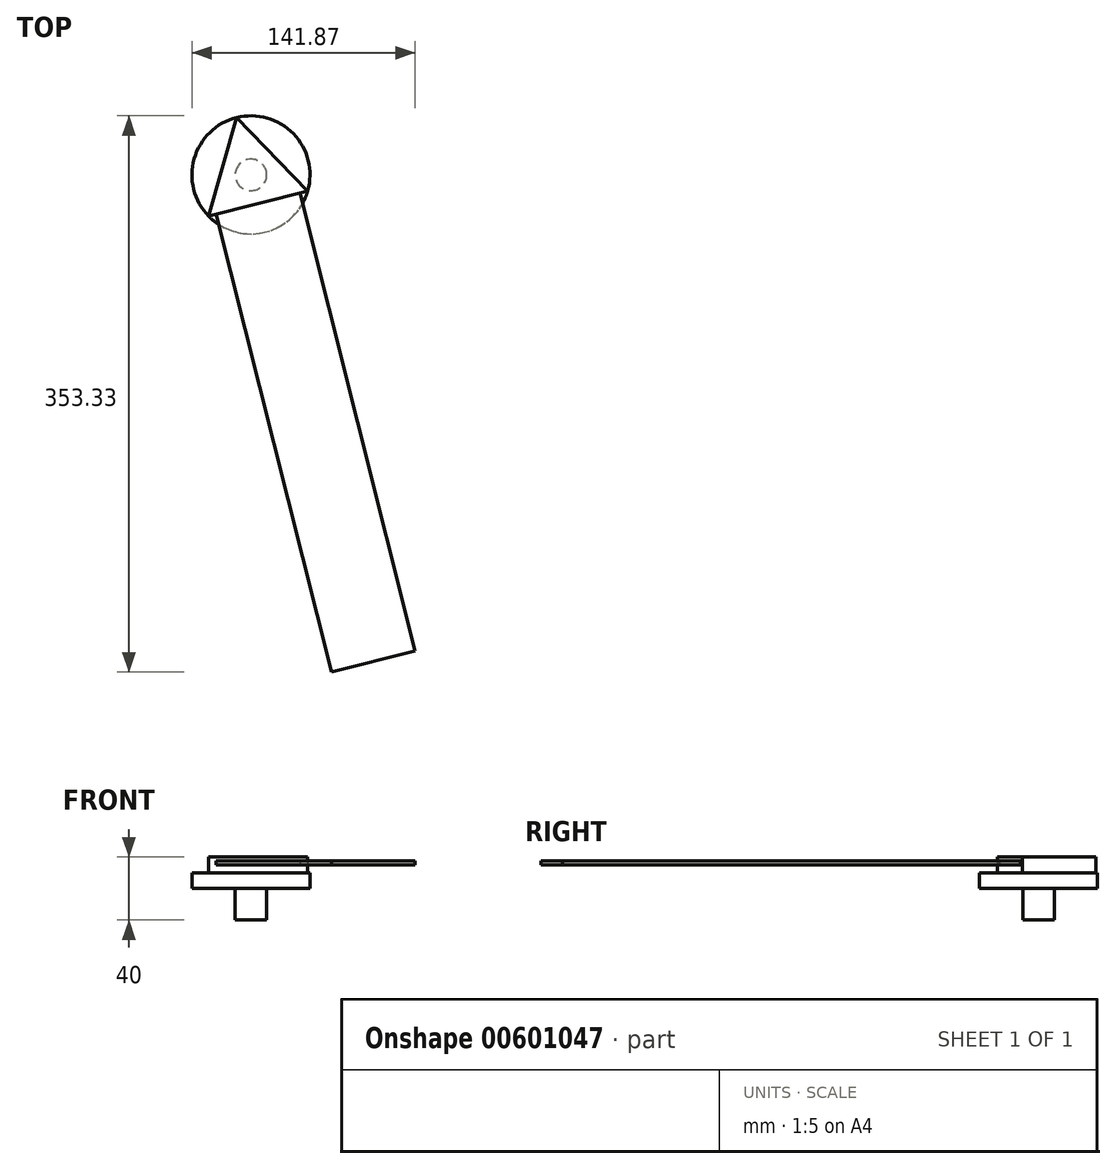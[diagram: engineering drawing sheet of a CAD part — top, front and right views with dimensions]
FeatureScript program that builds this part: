
annotation { "Feature Type Name" : "Feature", "Feature Type Description" : "" }
export const myFeature = defineFeature(function(context is Context, id is Id, definition is map)
    precondition{}
    {
        {
            var Q0;
            Q0=qCreatedBy(makeId("Top.planeOp"),FACE);
            var sketch = newSketch(context, id + "F0", { "sketchPlane" : qUnion([Q0])});
            skCircle(sketch, "E0", {"center": v(-117.09, -13.05) * mm, "radius": 37.5 * mm});
            skCircle(sketch, "E1", {"center": v(-117.09, -13.05) * mm, "radius": 10 * mm});
            skSolve(sketch);
        }
        {
            var Q0;
            Q0=makeQuery(id+"F0.imprint","IMPRINT",FACE,{"disambiguationData":[TD([[makeQuery(id+"F0.imprint","IMPRINT",EDGE,{"derivedFrom":sQuery(id+"F0.wireOp",EDGE,"E0")}),1.0]])]});
            var Q1;
            Q1=makeQuery(id+"F0.imprint","IMPRINT",FACE,{"disambiguationData":[TD([[makeQuery(id+"F0.imprint","IMPRINT",EDGE,{"derivedFrom":sQuery(id+"F0.wireOp",EDGE,"E1")}),1.0]])]});
            extrude(context, id + "F1", {"entities" : qUnion([Q0, Q1]), "depth" : 10 * mm, "offsetDistance" : 25 * mm});
        }
        {
            var Q0;
            Q0=makeQuery(id+"F1.opExtrude","CAP_FACE",FACE,{"disambiguationData":[OSD([sQuery(id+"F0.wireOp",EDGE,"E0")])],"isStart":false});
            var sketch = newSketch(context, id + "F2", { "sketchPlane" : qUnion([Q0])});
            skPoint(sketch, "E2.middle", {"position": v(-117.09, -13.05) * mm});
            skCircle(sketch, "E3.cCircle", {"center": v(-117.09, -13.05) * mm, "radius": 37.5 * mm, "construction": true});
            skLineSegment(sketch, "E3.0", {"start": v(-81.02, -23.32) * mm, "end": v(-144.01, -39.16) * mm});
            skLineSegment(sketch, "E3.1", {"start": v(-144.01, -39.16) * mm, "end": v(-126.23, 23.31) * mm});
            skLineSegment(sketch, "E3.2", {"start": v(-126.23, 23.31) * mm, "end": v(-81.02, -23.32) * mm});
            skSolve(sketch);
        }
        {
            var Q0;
            Q0 = qSketchRegion(id + "F2", true);
            extrude(context, id + "F3", {"entities" : qUnion([Q0]), "operationType" : NewBodyOperationType.ADD, "depth" : 10 * mm, "offsetDistance" : 25 * mm});
        }
        {
            var Q0;
            Q0=makeQuery(id+"F3.opExtrude","SWEPT_FACE",FACE,{"disambiguationData":[OSD([sQuery(id+"F2.wireOp",EDGE,"E3.0")])]});
            var sketch = newSketch(context, id + "F4", { "sketchPlane" : qUnion([Q0])});
            skLineSegment(sketch, "E4.bottom", {"start": v(-144.21, 15) * mm, "end": v(-89.26, 15) * mm});
            skLineSegment(sketch, "E4.top", {"start": v(-144.21, 17.5) * mm, "end": v(-89.26, 17.5) * mm});
            skLineSegment(sketch, "E4.left", {"start": v(-144.21, 17.5) * mm, "end": v(-144.21, 15) * mm});
            skLineSegment(sketch, "E4.right", {"start": v(-89.26, 17.5) * mm, "end": v(-89.26, 15) * mm});
            skSolve(sketch);
        }
        {
            var Q0;
            Q0 = qSketchRegion(id + "F4", true);
            extrude(context, id + "F5", {"entities" : qUnion([Q0]), "operationType" : NewBodyOperationType.ADD, "depth" : 300 * mm, "offsetDistance" : 25 * mm});
        }
        {
            var Q0;
            Q0=makeQuery(id+"F0.imprint","IMPRINT",FACE,{"disambiguationData":[TD([[makeQuery(id+"F0.imprint","IMPRINT",EDGE,{"derivedFrom":sQuery(id+"F0.wireOp",EDGE,"E1")}),1.0]])]});
            extrude(context, id + "F6", {"entities" : qUnion([Q0]), "operationType" : NewBodyOperationType.ADD, "oppositeDirection" : true, "depth" : 20 * mm, "offsetDistance" : 25 * mm});
        }
    });
